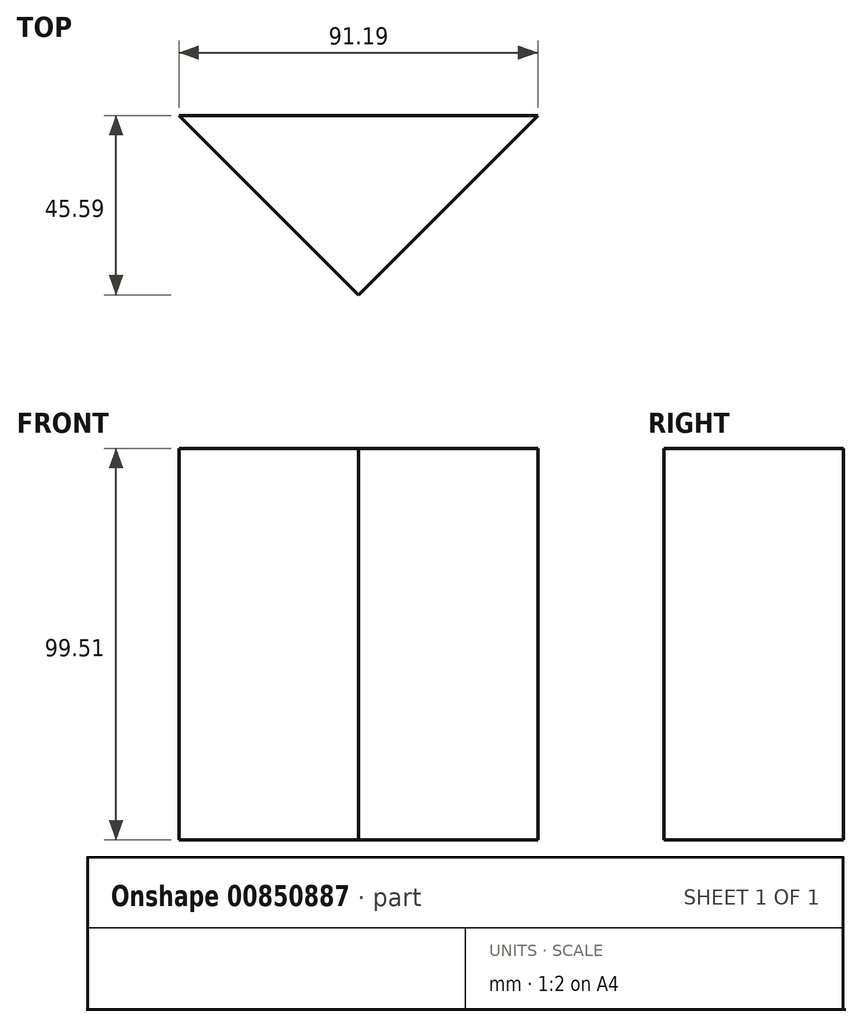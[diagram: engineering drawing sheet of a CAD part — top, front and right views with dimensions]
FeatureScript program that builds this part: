
annotation { "Feature Type Name" : "Feature", "Feature Type Description" : "" }
export const myFeature = defineFeature(function(context is Context, id is Id, definition is map)
    precondition{}
    {
        {
            var Q0;
            Q0=qCreatedBy(makeId("Front.planeOp"),FACE);
            var sketch = newSketch(context, id + "F0", { "sketchPlane" : qUnion([Q0])});
            skLineSegment(sketch, "E0.bottom", {"start": v(-38.9, 48.13) * mm, "end": v(52.29, 48.13) * mm});
            skLineSegment(sketch, "E0.top", {"start": v(-38.9, -51.38) * mm, "end": v(52.29, -51.38) * mm});
            skLineSegment(sketch, "E0.left", {"start": v(-38.9, 48.13) * mm, "end": v(-38.9, -51.38) * mm});
            skLineSegment(sketch, "E0.right", {"start": v(52.29, 48.13) * mm, "end": v(52.29, -51.38) * mm});
            skSolve(sketch);
        }
        {
            var Q0;
            Q0=makeQuery(id+"F0.imprint","IMPRINT",FACE,{"disambiguationData":[TD([[makeQuery(id+"F0.imprint","IMPRINT",EDGE,{"derivedFrom":sQuery(id+"F0.wireOp",EDGE,"E0.bottom")}),-1.0]])]});
            extrude(context, id + "F1", {"entities" : qUnion([Q0]), "depth" : 50.8 * mm, "offsetDistance" : 25.4 * mm});
        }
        {
            var Q0;
            Q0=makeQuery(id+"F1.opExtrude","CAP_EDGE",EDGE,{"disambiguationData":[OSD([sQuery(id+"F0.wireOp",EDGE,"E0.left")])],"isStart":false});
            var Q1;
            Q1=makeQuery(id+"F1.opExtrude","CAP_EDGE",EDGE,{"disambiguationData":[OSD([sQuery(id+"F0.wireOp",EDGE,"E0.right")])],"isStart":false});
            chamfer(context, id + "F2", {"entities" : qUnion([Q0, Q1]), "width" : 50.8 * mm, "tangentPropagation" : true});
        }
    });
